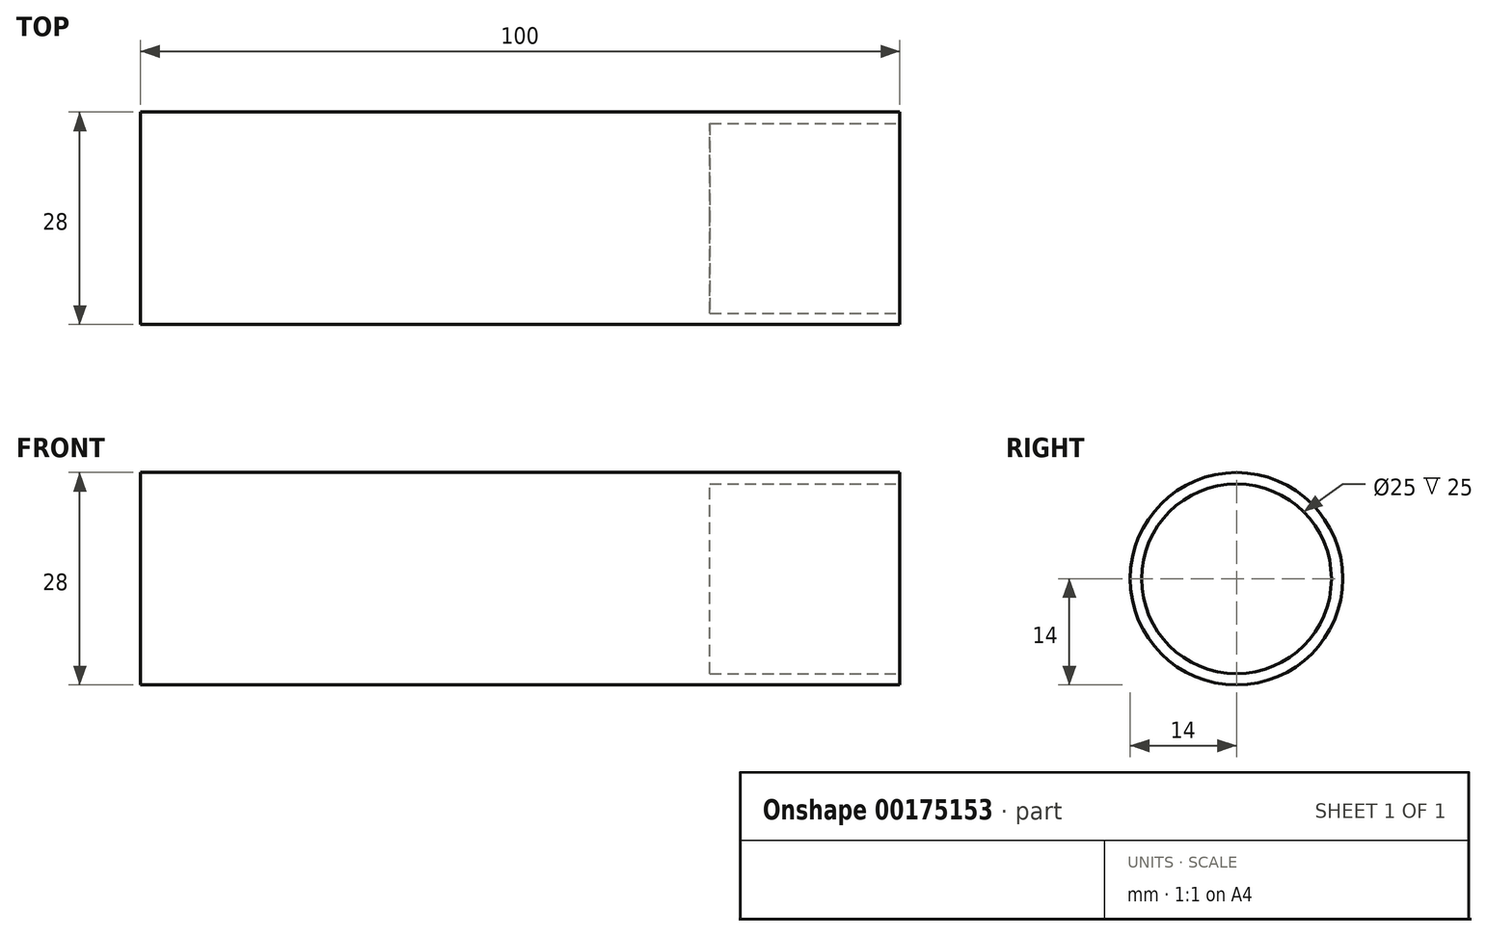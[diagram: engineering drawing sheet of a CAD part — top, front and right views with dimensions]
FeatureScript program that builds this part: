
annotation { "Feature Type Name" : "Feature", "Feature Type Description" : "" }
export const myFeature = defineFeature(function(context is Context, id is Id, definition is map)
    precondition{}
    {
        {
            var Q0;
            Q0=qCreatedBy(makeId("Right.planeOp"),FACE);
            var sketch = newSketch(context, id + "F0", { "sketchPlane" : qUnion([Q0])});
            skCircle(sketch, "E0", {"center": v(0, 0) * mm, "radius": 14 * mm});
            skSolve(sketch);
        }
        {
            var Q0;
            Q0=makeQuery(id+"F0.imprint","IMPRINT",FACE,{"disambiguationData":[TD([[makeQuery(id+"F0.imprint","IMPRINT",EDGE,{"derivedFrom":sQuery(id+"F0.wireOp",EDGE,"E0")}),1.0]])]});
            extrude(context, id + "F1", {"entities" : qUnion([Q0]), "oppositeDirection" : true, "depth" : 100 * mm});
        }
        {
            var Q0;
            Q0=qCreatedBy(makeId("Right.planeOp"),FACE);
            var sketch = newSketch(context, id + "F2", { "sketchPlane" : qUnion([Q0])});
            skCircle(sketch, "E1", {"center": v(0, 0) * mm, "radius": 12.5 * mm});
            skSolve(sketch);
        }
        {
            var Q0;
            Q0=makeQuery(id+"F2.imprint","IMPRINT",FACE,{"disambiguationData":[TD([[makeQuery(id+"F2.imprint","IMPRINT",EDGE,{"derivedFrom":sQuery(id+"F2.wireOp",EDGE,"E1")}),1.0]])]});
            extrude(context, id + "F3", {"entities" : qUnion([Q0]), "operationType" : NewBodyOperationType.REMOVE, "oppositeDirection" : true, "depth" : 25 * mm});
        }
    });
